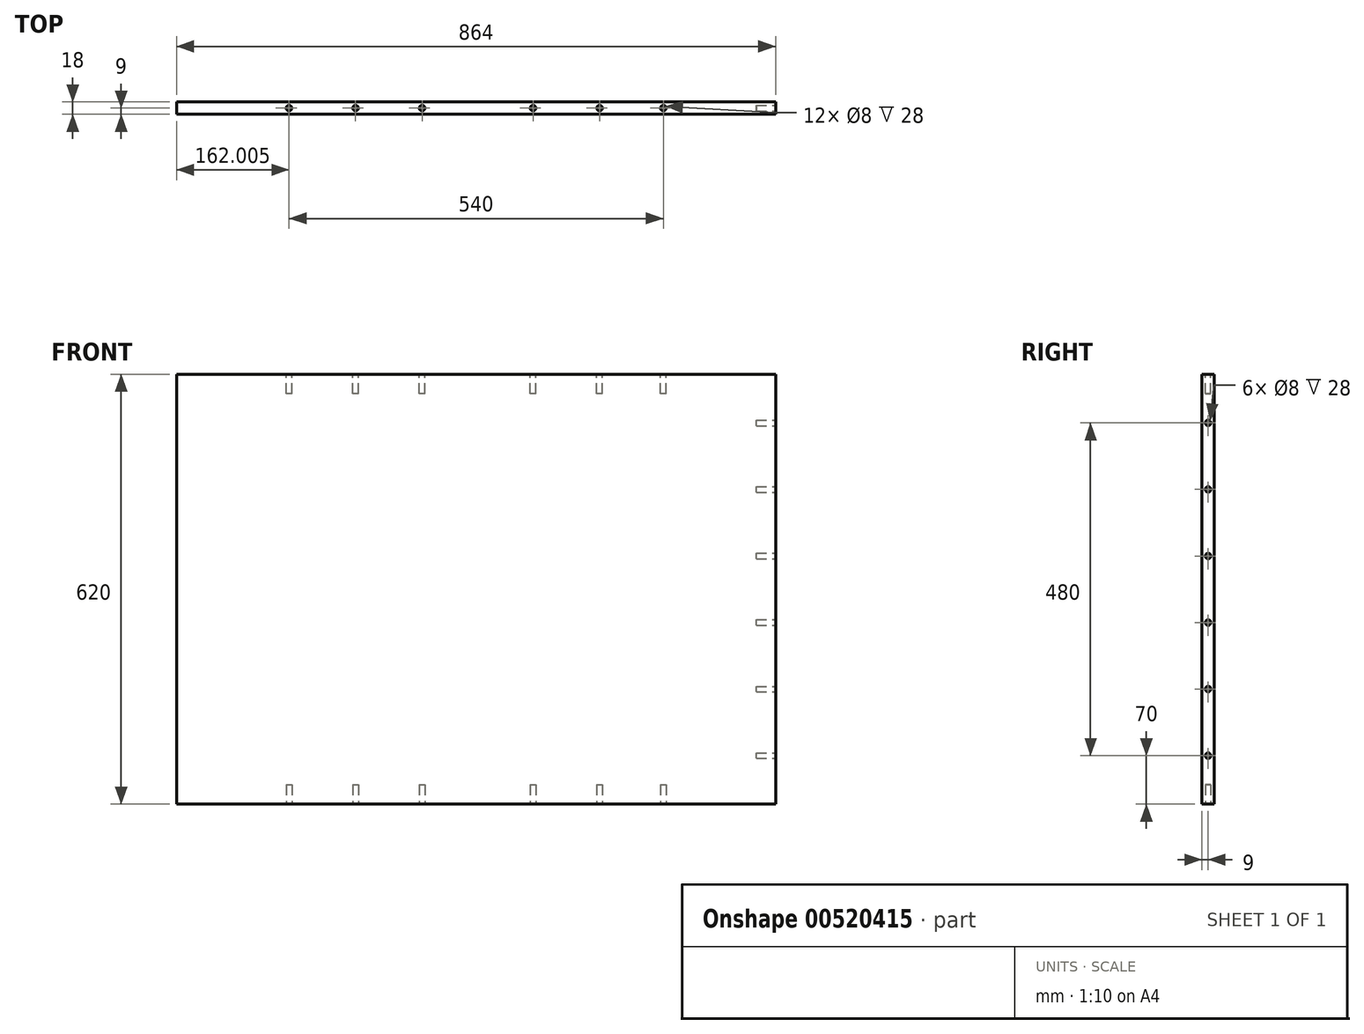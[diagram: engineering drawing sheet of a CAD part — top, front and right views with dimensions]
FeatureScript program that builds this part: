
annotation { "Feature Type Name" : "Feature", "Feature Type Description" : "" }
export const myFeature = defineFeature(function(context is Context, id is Id, definition is map)
    precondition{}
    {
        {
            var Q0;
            Q0=qCreatedBy(makeId("Top.planeOp"),FACE);
            var sketch = newSketch(context, id + "F0", { "sketchPlane" : qUnion([Q0])});
            skLineSegment(sketch, "E0.bottom", {"start": v(438.24, 9) * mm, "end": v(-425.76, 9) * mm});
            skLineSegment(sketch, "E0.top", {"start": v(438.24, -9) * mm, "end": v(-425.76, -9) * mm});
            skLineSegment(sketch, "E0.left", {"start": v(438.24, 9) * mm, "end": v(438.24, -9) * mm});
            skLineSegment(sketch, "E0.right", {"start": v(-425.76, 9) * mm, "end": v(-425.76, -9) * mm});
            skPoint(sketch, "E0.middle", {"position": v(6.24, 0) * mm});
            skSolve(sketch);
        }
        {
            var Q0;
            Q0=qSketchRegion(id+"F0",true);
            extrude(context, id + "F1", {"entities" : qUnion([Q0]), "depth" : 620 * mm, "offsetDistance" : 25 * mm});
        }
        {
            var Q0;
            Q0=makeQuery(id+"F1.opExtrude","CAP_FACE",FACE,{"disambiguationData":[OSD([sQuery(id+"F0.wireOp",EDGE,"E0.bottom"),sQuery(id+"F0.wireOp",EDGE,"E0.top"),sQuery(id+"F0.wireOp",EDGE,"E0.left"),sQuery(id+"F0.wireOp",EDGE,"E0.right")])],"isStart":true});
            var sketch = newSketch(context, id + "F2", { "sketchPlane" : qUnion([Q0])});
            skLineSegment(sketch, "E1", {"start": v(-263.76, 0) * mm, "end": v(276.24, 0) * mm, "construction": true});
            skCircle(sketch, "E2", {"center": v(-263.76, 0) * mm, "radius": 4 * mm});
            skCircle(sketch, "E3", {"center": v(-167.76, 0) * mm, "radius": 4 * mm});
            skCircle(sketch, "E4", {"center": v(-71.76, 0) * mm, "radius": 4 * mm});
            skCircle(sketch, "E5", {"center": v(88.24, 0) * mm, "radius": 4 * mm});
            skCircle(sketch, "E6", {"center": v(276.24, 0) * mm, "radius": 4 * mm});
            skCircle(sketch, "E7", {"center": v(184.24, 0) * mm, "radius": 4 * mm});
            skLineSegment(sketch, "E8", {"start": v(6.24, 9) * mm, "end": v(6.24, 0) * mm, "construction": true});
            skSolve(sketch);
        }
        {
            var Q0;
            Q0=qSketchRegion(id+"F2",true);
            extrude(context, id + "F3", {"entities" : qUnion([Q0]), "operationType" : NewBodyOperationType.REMOVE, "oppositeDirection" : true, "depth" : 28 * mm, "offsetDistance" : 25 * mm});
        }
        {
            var Q0;
            Q0=makeQuery(id+"F1.opExtrude","CAP_FACE",FACE,{"disambiguationData":[OSD([sQuery(id+"F0.wireOp",EDGE,"E0.bottom"),sQuery(id+"F0.wireOp",EDGE,"E0.top"),sQuery(id+"F0.wireOp",EDGE,"E0.left"),sQuery(id+"F0.wireOp",EDGE,"E0.right")])],"isStart":false});
            var sketch = newSketch(context, id + "F4", { "sketchPlane" : qUnion([Q0])});
            skLineSegment(sketch, "E9.1", {"start": v(-263.76, 0) * mm, "end": v(276.24, 0) * mm, "construction": true});
            skCircle(sketch, "E9.2", {"center": v(-263.76, 0) * mm, "radius": 4 * mm});
            skCircle(sketch, "E9.3", {"center": v(-167.76, 0) * mm, "radius": 4 * mm});
            skCircle(sketch, "E9.4", {"center": v(-71.76, 0) * mm, "radius": 4 * mm});
            skCircle(sketch, "E9.5", {"center": v(88.24, 0) * mm, "radius": 4 * mm});
            skCircle(sketch, "E9.6", {"center": v(276.24, 0) * mm, "radius": 4 * mm});
            skCircle(sketch, "E9.7", {"center": v(184.24, 0) * mm, "radius": 4 * mm});
            skSolve(sketch);
        }
        {
            var Q0;
            Q0=qSketchRegion(id+"F4",true);
            extrude(context, id + "F5", {"entities" : qUnion([Q0]), "operationType" : NewBodyOperationType.REMOVE, "oppositeDirection" : true, "depth" : 28 * mm, "offsetDistance" : 25 * mm});
        }
        {
            var Q0;
            Q0=makeQuery(id+"F1.opExtrude","SWEPT_FACE",FACE,{"disambiguationData":[OSD([sQuery(id+"F0.wireOp",EDGE,"E0.left")])]});
            var sketch = newSketch(context, id + "F6", { "sketchPlane" : qUnion([Q0])});
            skLineSegment(sketch, "E10", {"start": v(0, 550) * mm, "end": v(0, 70) * mm, "construction": true});
            skLineSegment(sketch, "E11", {"start": v(0, 310) * mm, "end": v(-9, 310) * mm, "construction": true});
            skCircle(sketch, "E12", {"center": v(0, 550) * mm, "radius": 4 * mm});
            skCircle(sketch, "E13.0.1.0", {"center": v(0, 518) * mm, "radius": 4 * mm, "construction": true});
            skCircle(sketch, "E13.0.2.0", {"center": v(0, 486) * mm, "radius": 4 * mm, "construction": true});
            skCircle(sketch, "E13.0.3.0", {"center": v(0, 454) * mm, "radius": 4 * mm});
            skCircle(sketch, "E13.0.4.0", {"center": v(0, 422) * mm, "radius": 4 * mm, "construction": true});
            skCircle(sketch, "E13.0.5.0", {"center": v(0, 390) * mm, "radius": 4 * mm, "construction": true});
            skCircle(sketch, "E13.0.6.0", {"center": v(0, 358) * mm, "radius": 4 * mm});
            skCircle(sketch, "E13.0.7.0", {"center": v(0, 326) * mm, "radius": 4 * mm, "construction": true});
            skCircle(sketch, "E13.0.8.0", {"center": v(0, 294) * mm, "radius": 4 * mm, "construction": true});
            skCircle(sketch, "E13.0.9.0", {"center": v(0, 262) * mm, "radius": 4 * mm});
            skCircle(sketch, "E13.0.10.0", {"center": v(0, 230) * mm, "radius": 4 * mm, "construction": true});
            skCircle(sketch, "E13.0.11.0", {"center": v(0, 198) * mm, "radius": 4 * mm, "construction": true});
            skCircle(sketch, "E13.0.12.0", {"center": v(0, 166) * mm, "radius": 4 * mm});
            skCircle(sketch, "E13.0.13.0", {"center": v(0, 134) * mm, "radius": 4 * mm, "construction": true});
            skCircle(sketch, "E13.0.14.0", {"center": v(0, 102) * mm, "radius": 4 * mm, "construction": true});
            skCircle(sketch, "E13.0.15.0", {"center": v(0, 70) * mm, "radius": 4 * mm});
            skLineSegment(sketch, "E13.direction1", {"start": v(0, 550) * mm, "end": v(15, 550) * mm, "construction": true});
            skLineSegment(sketch, "E13.direction2", {"start": v(0, 550) * mm, "end": v(0, 518) * mm, "construction": true});
            skLineSegment(sketch, "E14", {"start": v(0, 550) * mm, "end": v(0, 620) * mm, "construction": true});
            skSolve(sketch);
        }
        {
            var Q0;
            Q0=qSketchRegion(id+"F6",true);
            extrude(context, id + "F7", {"entities" : qUnion([Q0]), "operationType" : NewBodyOperationType.REMOVE, "oppositeDirection" : true, "depth" : 28 * mm, "offsetDistance" : 25 * mm});
        }
        {
            var Q0;
            Q0=makeQuery(id+"F1.opExtrude","SWEPT_FACE",FACE,{"disambiguationData":[OSD([sQuery(id+"F0.wireOp",EDGE,"E0.right")])]});
            var sketch = newSketch(context, id + "F8", { "sketchPlane" : qUnion([Q0])});
            skCircle(sketch, "E15.2", {"center": v(0, 550) * mm, "radius": 4 * mm});
            skCircle(sketch, "E15.3", {"center": v(0, 518) * mm, "radius": 4 * mm, "construction": true});
            skCircle(sketch, "E15.4", {"center": v(0, 486) * mm, "radius": 4 * mm, "construction": true});
            skCircle(sketch, "E15.5", {"center": v(0, 454) * mm, "radius": 4 * mm});
            skCircle(sketch, "E15.6", {"center": v(0, 422) * mm, "radius": 4 * mm, "construction": true});
            skCircle(sketch, "E15.7", {"center": v(0, 390) * mm, "radius": 4 * mm, "construction": true});
            skCircle(sketch, "E15.8", {"center": v(0, 358) * mm, "radius": 4 * mm});
            skCircle(sketch, "E15.9", {"center": v(0, 326) * mm, "radius": 4 * mm, "construction": true});
            skCircle(sketch, "E15.10", {"center": v(0, 294) * mm, "radius": 4 * mm, "construction": true});
            skCircle(sketch, "E15.11", {"center": v(0, 262) * mm, "radius": 4 * mm});
            skCircle(sketch, "E15.12", {"center": v(0, 230) * mm, "radius": 4 * mm, "construction": true});
            skCircle(sketch, "E15.13", {"center": v(0, 198) * mm, "radius": 4 * mm, "construction": true});
            skCircle(sketch, "E15.14", {"center": v(0, 166) * mm, "radius": 4 * mm});
            skCircle(sketch, "E15.15", {"center": v(0, 134) * mm, "radius": 4 * mm, "construction": true});
            skCircle(sketch, "E15.16", {"center": v(0, 102) * mm, "radius": 4 * mm, "construction": true});
            skCircle(sketch, "E15.17", {"center": v(0, 70) * mm, "radius": 4 * mm});
            skSolve(sketch);
        }
        {
            var Q0;
            Q0 = qSketchRegion(id + "F8", true);
            extrude(context, id + "F9", {"entities" : qUnion([Q0]), "operationType" : NewBodyOperationType.ADD, "oppositeDirection" : true, "depth" : 28 * mm, "offsetDistance" : 25 * mm});
        }
    });
